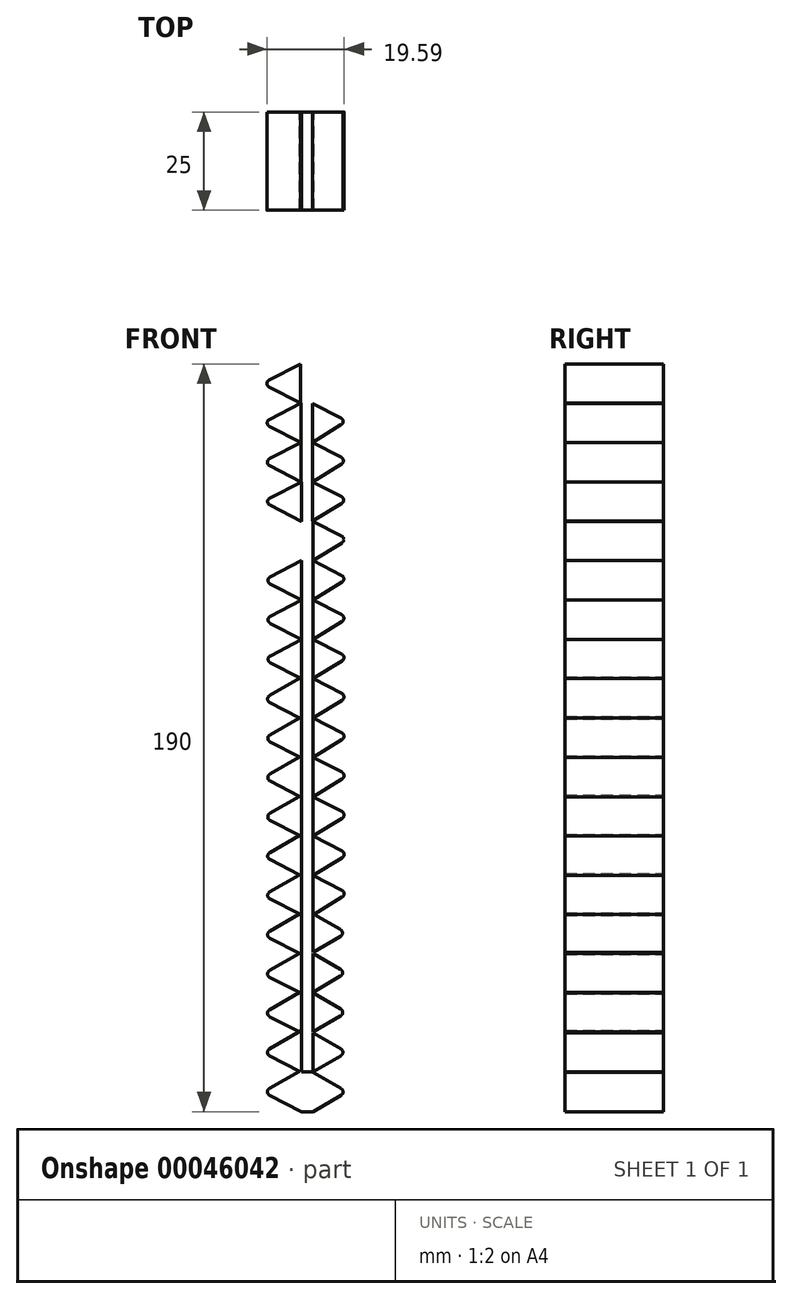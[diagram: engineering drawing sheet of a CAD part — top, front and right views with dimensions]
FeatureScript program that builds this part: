
annotation { "Feature Type Name" : "Feature", "Feature Type Description" : "" }
export const myFeature = defineFeature(function(context is Context, id is Id, definition is map)
    precondition{}
    {
        {
            var Q0;
            Q0=qCreatedBy(makeId("Front.planeOp"),FACE);
            var sketch = newSketch(context, id + "F0", { "sketchPlane" : qUnion([Q0])});
            skLineSegment(sketch, "E0.right", {"start": v(-51.03, -7.28) * mm, "end": v(-51.03, -157.28) * mm});
            skLineSegment(sketch, "E1", {"start": v(-51.03, -157.28) * mm, "end": v(-60.8, -152.28) * mm});
            skLineSegment(sketch, "E2", {"start": v(-60.8, -152.28) * mm, "end": v(-51.03, -146.64) * mm});
            skLineSegment(sketch, "E3.1.0.0", {"start": v(-60.8, -142.3) * mm, "end": v(-51.02, -136.66) * mm});
            skLineSegment(sketch, "E3.1.0.1", {"start": v(-51.02, -147.3) * mm, "end": v(-60.8, -142.3) * mm});
            skLineSegment(sketch, "E3.2.0.0", {"start": v(-60.78, -132.32) * mm, "end": v(-51, -126.68) * mm});
            skLineSegment(sketch, "E3.2.0.1", {"start": v(-51, -137.32) * mm, "end": v(-60.78, -132.32) * mm});
            skLineSegment(sketch, "E3.3.0.0", {"start": v(-60.77, -122.35) * mm, "end": v(-51, -116.7) * mm});
            skLineSegment(sketch, "E3.3.0.1", {"start": v(-51, -127.35) * mm, "end": v(-60.77, -122.35) * mm});
            skLineSegment(sketch, "E3.4.0.0", {"start": v(-60.76, -112.37) * mm, "end": v(-50.99, -106.72) * mm});
            skLineSegment(sketch, "E3.4.0.1", {"start": v(-50.99, -117.37) * mm, "end": v(-60.76, -112.37) * mm});
            skLineSegment(sketch, "E3.5.0.0", {"start": v(-60.75, -102.39) * mm, "end": v(-50.98, -96.75) * mm});
            skLineSegment(sketch, "E3.5.0.1", {"start": v(-50.98, -107.39) * mm, "end": v(-60.75, -102.39) * mm});
            skLineSegment(sketch, "E3.6.0.0", {"start": v(-60.74, -92.4) * mm, "end": v(-50.97, -86.77) * mm});
            skLineSegment(sketch, "E3.6.0.1", {"start": v(-50.97, -97.4) * mm, "end": v(-60.74, -92.4) * mm});
            skLineSegment(sketch, "E3.7.0.0", {"start": v(-60.73, -82.43) * mm, "end": v(-50.95, -76.79) * mm});
            skLineSegment(sketch, "E3.7.0.1", {"start": v(-50.95, -87.43) * mm, "end": v(-60.73, -82.43) * mm});
            skLineSegment(sketch, "E3.8.0.0", {"start": v(-60.72, -72.45) * mm, "end": v(-50.94, -66.8) * mm});
            skLineSegment(sketch, "E3.8.0.1", {"start": v(-50.94, -77.45) * mm, "end": v(-60.72, -72.45) * mm});
            skLineSegment(sketch, "E3.9.0.0", {"start": v(-60.7, -62.47) * mm, "end": v(-50.93, -56.83) * mm});
            skLineSegment(sketch, "E3.9.0.1", {"start": v(-50.93, -67.47) * mm, "end": v(-60.7, -62.47) * mm});
            skLineSegment(sketch, "E3.direction1", {"start": v(-60.8, -152.28) * mm, "end": v(-60.8, -142.3) * mm, "construction": true});
            skLineSegment(sketch, "E4.1.0.0", {"start": v(-60.77, -52.5) * mm, "end": v(-51, -46.86) * mm});
            skLineSegment(sketch, "E4.1.0.1", {"start": v(-51, -57.5) * mm, "end": v(-60.77, -52.5) * mm});
            skLineSegment(sketch, "E4.direction1", {"start": v(-60.7, -62.47) * mm, "end": v(-60.77, -52.5) * mm, "construction": true});
            skLineSegment(sketch, "E5", {"start": v(-51.03, -7.28) * mm, "end": v(-51.03, -17.28) * mm});
            skLineSegment(sketch, "E6", {"start": v(-51.03, -17.28) * mm, "end": v(-60.8, -12.28) * mm});
            skLineSegment(sketch, "E7", {"start": v(-60.8, -12.28) * mm, "end": v(-51.03, -7.28) * mm});
            skLineSegment(sketch, "E8", {"start": v(-51.03, -7.28) * mm, "end": v(-48.18, -7.28) * mm});
            skLineSegment(sketch, "E9", {"start": v(-48.18, -7.28) * mm, "end": v(-48.18, -157.28) * mm});
            skLineSegment(sketch, "E10", {"start": v(-48.18, -157.28) * mm, "end": v(-51.03, -157.28) * mm});
            skLineSegment(sketch, "E11", {"start": v(-48.18, -7.28) * mm, "end": v(-39.28, -11.84) * mm});
            skLineSegment(sketch, "E12", {"start": v(-39.28, -11.84) * mm, "end": v(-48.18, -17.28) * mm});
            skLineSegment(sketch, "E13", {"start": v(-48.18, -17.28) * mm, "end": v(-48.18, -7.28) * mm});
            skLineSegment(sketch, "E14.1.0.0", {"start": v(-48.18, -27.28) * mm, "end": v(-48.18, -17.28) * mm});
            skLineSegment(sketch, "E14.1.0.1", {"start": v(-48.18, -17.28) * mm, "end": v(-39.27, -21.84) * mm});
            skLineSegment(sketch, "E14.1.0.2", {"start": v(-39.27, -21.84) * mm, "end": v(-48.18, -27.28) * mm});
            skLineSegment(sketch, "E14.2.0.0", {"start": v(-48.17, -37.28) * mm, "end": v(-48.17, -27.28) * mm});
            skLineSegment(sketch, "E14.2.0.1", {"start": v(-48.17, -27.28) * mm, "end": v(-39.27, -31.84) * mm});
            skLineSegment(sketch, "E14.2.0.2", {"start": v(-39.27, -31.84) * mm, "end": v(-48.17, -37.28) * mm});
            skLineSegment(sketch, "E14.3.0.0", {"start": v(-48.16, -47.28) * mm, "end": v(-48.16, -37.28) * mm});
            skLineSegment(sketch, "E14.3.0.1", {"start": v(-48.16, -37.28) * mm, "end": v(-39.26, -41.84) * mm});
            skLineSegment(sketch, "E14.3.0.2", {"start": v(-39.26, -41.84) * mm, "end": v(-48.16, -47.28) * mm});
            skLineSegment(sketch, "E14.4.0.0", {"start": v(-48.15, -57.28) * mm, "end": v(-48.15, -47.28) * mm});
            skLineSegment(sketch, "E14.4.0.1", {"start": v(-48.15, -47.28) * mm, "end": v(-39.25, -51.84) * mm});
            skLineSegment(sketch, "E14.4.0.2", {"start": v(-39.25, -51.84) * mm, "end": v(-48.15, -57.28) * mm});
            skLineSegment(sketch, "E14.5.0.0", {"start": v(-48.14, -67.28) * mm, "end": v(-48.14, -57.28) * mm});
            skLineSegment(sketch, "E14.5.0.1", {"start": v(-48.14, -57.28) * mm, "end": v(-39.24, -61.84) * mm});
            skLineSegment(sketch, "E14.5.0.2", {"start": v(-39.24, -61.84) * mm, "end": v(-48.14, -67.28) * mm});
            skLineSegment(sketch, "E14.6.0.0", {"start": v(-48.14, -77.28) * mm, "end": v(-48.14, -67.28) * mm});
            skLineSegment(sketch, "E14.6.0.1", {"start": v(-48.14, -67.28) * mm, "end": v(-39.23, -71.84) * mm});
            skLineSegment(sketch, "E14.6.0.2", {"start": v(-39.23, -71.84) * mm, "end": v(-48.14, -77.28) * mm});
            skLineSegment(sketch, "E14.7.0.0", {"start": v(-48.13, -87.28) * mm, "end": v(-48.13, -77.28) * mm});
            skLineSegment(sketch, "E14.7.0.1", {"start": v(-48.13, -77.28) * mm, "end": v(-39.23, -81.84) * mm});
            skLineSegment(sketch, "E14.7.0.2", {"start": v(-39.23, -81.84) * mm, "end": v(-48.13, -87.28) * mm});
            skLineSegment(sketch, "E14.8.0.0", {"start": v(-48.12, -97.28) * mm, "end": v(-48.12, -87.28) * mm});
            skLineSegment(sketch, "E14.8.0.1", {"start": v(-48.12, -87.28) * mm, "end": v(-39.22, -91.84) * mm});
            skLineSegment(sketch, "E14.8.0.2", {"start": v(-39.22, -91.84) * mm, "end": v(-48.12, -97.28) * mm});
            skLineSegment(sketch, "E14.9.0.0", {"start": v(-48.11, -107.28) * mm, "end": v(-48.11, -97.28) * mm});
            skLineSegment(sketch, "E14.9.0.1", {"start": v(-48.11, -97.28) * mm, "end": v(-39.21, -101.84) * mm});
            skLineSegment(sketch, "E14.9.0.2", {"start": v(-39.21, -101.84) * mm, "end": v(-48.11, -107.28) * mm});
            skLineSegment(sketch, "E14.direction1", {"start": v(-48.18, -17.28) * mm, "end": v(-48.18, -27.28) * mm, "construction": true});
            skLineSegment(sketch, "E15", {"start": v(-48.18, -157.28) * mm, "end": v(-39.52, -152.28) * mm});
            skLineSegment(sketch, "E16", {"start": v(-39.52, -152.28) * mm, "end": v(-48.18, -147.3) * mm});
            skLineSegment(sketch, "E17", {"start": v(-48.18, -147.3) * mm, "end": v(-48.18, -157.28) * mm});
            skLineSegment(sketch, "E18.1.0.0", {"start": v(-48.22, -147.18) * mm, "end": v(-51.06, -147.18) * mm});
            skLineSegment(sketch, "E18.1.0.1", {"start": v(-48.22, -147.18) * mm, "end": v(-39.56, -142.18) * mm});
            skLineSegment(sketch, "E18.1.0.2", {"start": v(-48.22, 2.82) * mm, "end": v(-48.22, -147.18) * mm});
            skLineSegment(sketch, "E18.1.0.3", {"start": v(-39.56, -142.18) * mm, "end": v(-48.22, -137.2) * mm});
            skLineSegment(sketch, "E18.1.0.4", {"start": v(-48.22, -137.2) * mm, "end": v(-48.22, -147.18) * mm});
            skLineSegment(sketch, "E18.2.0.0", {"start": v(-48.26, -137.08) * mm, "end": v(-51.1, -137.08) * mm});
            skLineSegment(sketch, "E18.2.0.1", {"start": v(-48.26, -137.08) * mm, "end": v(-39.6, -132.08) * mm});
            skLineSegment(sketch, "E18.2.0.2", {"start": v(-48.26, 12.92) * mm, "end": v(-48.26, -137.08) * mm});
            skLineSegment(sketch, "E18.2.0.3", {"start": v(-39.6, -132.08) * mm, "end": v(-48.26, -127.1) * mm});
            skLineSegment(sketch, "E18.2.0.4", {"start": v(-48.26, -127.1) * mm, "end": v(-48.26, -137.08) * mm});
            skLineSegment(sketch, "E18.3.0.0", {"start": v(-48.3, -126.98) * mm, "end": v(-51.13, -126.98) * mm});
            skLineSegment(sketch, "E18.3.0.1", {"start": v(-48.3, -126.98) * mm, "end": v(-39.63, -121.98) * mm});
            skLineSegment(sketch, "E18.3.0.2", {"start": v(-48.3, 23.02) * mm, "end": v(-48.3, -126.98) * mm});
            skLineSegment(sketch, "E18.3.0.3", {"start": v(-39.63, -121.98) * mm, "end": v(-48.3, -117) * mm});
            skLineSegment(sketch, "E18.3.0.4", {"start": v(-48.3, -117) * mm, "end": v(-48.3, -126.98) * mm});
            skLineSegment(sketch, "E18.4.0.0", {"start": v(-48.33, -116.88) * mm, "end": v(-51.17, -116.88) * mm});
            skLineSegment(sketch, "E18.4.0.1", {"start": v(-48.33, -116.88) * mm, "end": v(-39.67, -111.88) * mm});
            skLineSegment(sketch, "E18.4.0.2", {"start": v(-48.33, 33.12) * mm, "end": v(-48.33, -116.88) * mm});
            skLineSegment(sketch, "E18.4.0.3", {"start": v(-39.67, -111.88) * mm, "end": v(-48.33, -106.9) * mm});
            skLineSegment(sketch, "E18.4.0.4", {"start": v(-48.33, -106.9) * mm, "end": v(-48.33, -116.88) * mm});
            skLineSegment(sketch, "E18.direction1", {"start": v(-51.03, -157.28) * mm, "end": v(-51.06, -147.18) * mm, "construction": true});
            skLineSegment(sketch, "E19.1.0.0", {"start": v(-51, -27.3) * mm, "end": v(-60.78, -22.3) * mm});
            skLineSegment(sketch, "E19.1.0.1", {"start": v(-60.78, -22.3) * mm, "end": v(-51, -17.3) * mm});
            skLineSegment(sketch, "E19.1.0.2", {"start": v(-51, -17.3) * mm, "end": v(-51, -27.3) * mm});
            skLineSegment(sketch, "E19.2.0.0", {"start": v(-50.98, -37.32) * mm, "end": v(-60.76, -32.32) * mm});
            skLineSegment(sketch, "E19.2.0.1", {"start": v(-60.76, -32.32) * mm, "end": v(-50.98, -27.32) * mm});
            skLineSegment(sketch, "E19.2.0.2", {"start": v(-50.98, -27.32) * mm, "end": v(-50.98, -37.32) * mm});
            skLineSegment(sketch, "E19.3.0.0", {"start": v(-50.96, -47.34) * mm, "end": v(-60.73, -42.34) * mm});
            skLineSegment(sketch, "E19.3.0.1", {"start": v(-60.73, -42.34) * mm, "end": v(-50.96, -37.34) * mm});
            skLineSegment(sketch, "E19.3.0.2", {"start": v(-50.96, -37.34) * mm, "end": v(-50.96, -47.34) * mm});
            skLineSegment(sketch, "E19.direction1", {"start": v(-60.8, -12.28) * mm, "end": v(-60.78, -22.3) * mm, "construction": true});
            skLineSegment(sketch, "E20.bottom", {"start": v(-51.03, -7.28) * mm, "end": v(-48.33, -7.28) * mm});
            skLineSegment(sketch, "E20.top", {"start": v(-51.03, 33.12) * mm, "end": v(-48.33, 33.12) * mm});
            skLineSegment(sketch, "E20.left", {"start": v(-51.03, -7.28) * mm, "end": v(-51.03, 33.12) * mm});
            skLineSegment(sketch, "E20.right", {"start": v(-48.33, -7.28) * mm, "end": v(-48.33, 33.12) * mm});
            skLineSegment(sketch, "E21.1.0.0", {"start": v(-48.24, 2.72) * mm, "end": v(-39.34, -1.84) * mm});
            skLineSegment(sketch, "E21.1.0.1", {"start": v(-39.34, -1.84) * mm, "end": v(-48.24, -7.28) * mm});
            skLineSegment(sketch, "E21.1.0.2", {"start": v(-48.24, -7.28) * mm, "end": v(-48.24, 2.72) * mm});
            skLineSegment(sketch, "E21.1.0.3", {"start": v(-51.09, 2.72) * mm, "end": v(-51.09, -7.28) * mm});
            skLineSegment(sketch, "E21.1.0.4", {"start": v(-60.86, -2.28) * mm, "end": v(-51.09, 2.72) * mm});
            skLineSegment(sketch, "E21.1.0.5", {"start": v(-51.09, -7.28) * mm, "end": v(-60.86, -2.28) * mm});
            skLineSegment(sketch, "E21.1.0.6", {"start": v(-51.09, 2.72) * mm, "end": v(-48.39, 2.72) * mm});
            skLineSegment(sketch, "E21.1.0.7", {"start": v(-51.09, 2.72) * mm, "end": v(-48.24, 2.72) * mm});
            skLineSegment(sketch, "E21.2.0.0", {"start": v(-48.3, 12.72) * mm, "end": v(-39.4, 8.16) * mm});
            skLineSegment(sketch, "E21.2.0.1", {"start": v(-39.4, 8.16) * mm, "end": v(-48.3, 2.72) * mm});
            skLineSegment(sketch, "E21.2.0.2", {"start": v(-48.3, 2.72) * mm, "end": v(-48.3, 12.72) * mm});
            skLineSegment(sketch, "E21.2.0.3", {"start": v(-51.14, 12.72) * mm, "end": v(-51.14, 2.72) * mm});
            skLineSegment(sketch, "E21.2.0.4", {"start": v(-60.92, 7.72) * mm, "end": v(-51.14, 12.72) * mm});
            skLineSegment(sketch, "E21.2.0.5", {"start": v(-51.14, 2.72) * mm, "end": v(-60.92, 7.72) * mm});
            skLineSegment(sketch, "E21.2.0.6", {"start": v(-51.14, 12.72) * mm, "end": v(-48.44, 12.72) * mm});
            skLineSegment(sketch, "E21.2.0.7", {"start": v(-51.14, 12.72) * mm, "end": v(-48.3, 12.72) * mm});
            skLineSegment(sketch, "E21.3.0.0", {"start": v(-48.36, 22.72) * mm, "end": v(-39.46, 18.16) * mm});
            skLineSegment(sketch, "E21.3.0.1", {"start": v(-39.46, 18.16) * mm, "end": v(-48.36, 12.72) * mm});
            skLineSegment(sketch, "E21.3.0.2", {"start": v(-48.36, 12.72) * mm, "end": v(-48.36, 22.72) * mm});
            skLineSegment(sketch, "E21.3.0.3", {"start": v(-51.2, 22.72) * mm, "end": v(-51.2, 12.72) * mm});
            skLineSegment(sketch, "E21.3.0.4", {"start": v(-60.98, 17.72) * mm, "end": v(-51.2, 22.72) * mm});
            skLineSegment(sketch, "E21.3.0.5", {"start": v(-51.2, 12.72) * mm, "end": v(-60.98, 17.72) * mm});
            skLineSegment(sketch, "E21.3.0.6", {"start": v(-51.2, 22.72) * mm, "end": v(-48.5, 22.72) * mm});
            skLineSegment(sketch, "E21.3.0.7", {"start": v(-51.2, 22.72) * mm, "end": v(-48.36, 22.72) * mm});
            skLineSegment(sketch, "E21.4.0.0", {"start": v(-48.42, 32.72) * mm, "end": v(-39.51, 28.16) * mm});
            skLineSegment(sketch, "E21.4.0.1", {"start": v(-39.51, 28.16) * mm, "end": v(-48.42, 22.72) * mm});
            skLineSegment(sketch, "E21.4.0.2", {"start": v(-48.42, 22.72) * mm, "end": v(-48.42, 32.72) * mm});
            skLineSegment(sketch, "E21.4.0.3", {"start": v(-51.26, 32.72) * mm, "end": v(-51.26, 22.72) * mm});
            skLineSegment(sketch, "E21.4.0.4", {"start": v(-61.03, 27.72) * mm, "end": v(-51.26, 32.72) * mm});
            skLineSegment(sketch, "E21.4.0.5", {"start": v(-51.26, 22.72) * mm, "end": v(-61.03, 27.72) * mm});
            skLineSegment(sketch, "E21.4.0.6", {"start": v(-51.26, 32.72) * mm, "end": v(-48.56, 32.72) * mm});
            skLineSegment(sketch, "E21.4.0.7", {"start": v(-51.26, 32.72) * mm, "end": v(-48.42, 32.72) * mm});
            skLineSegment(sketch, "E21.direction1", {"start": v(-48.18, -7.28) * mm, "end": v(-48.24, 2.72) * mm, "construction": true});
            skSolve(sketch);
        }
        {
            var Q0;
            {var subQ1=sQuery(id+"F0.wireOp",EDGE,"E5");Q0=makeQuery(id+"F0.imprint","IMPRINT",FACE,{"disambiguationData":[TD([[makeQuery(id+"F0.imprint","IMPRINT",EDGE,{"derivedFrom":subQ1}),1.0]])]});}
            var Q1;
            {var subQ8=sQuery(id+"F0.wireOp",EDGE,"E18.3.0.4");Q1=makeQuery(id+"F0.imprint","IMPRINT",FACE,{"disambiguationData":[TD([[makeQuery(id+"F0.imprint","IMPRINT",EDGE,{"derivedFrom":subQ8}),-1.0]])]});}
            var Q2;
            {var subQ5=sQuery(id+"F0.wireOp",EDGE,"E18.2.0.4");Q2=makeQuery(id+"F0.imprint","IMPRINT",FACE,{"disambiguationData":[TD([[makeQuery(id+"F0.imprint","IMPRINT",EDGE,{"derivedFrom":subQ5}),-1.0]])]});}
            var Q3;
            {var subQ0=sQuery(id+"F0.wireOp",EDGE,"E18.1.0.4");Q3=makeQuery(id+"F0.imprint","IMPRINT",FACE,{"disambiguationData":[TD([[makeQuery(id+"F0.imprint","IMPRINT",EDGE,{"derivedFrom":subQ0}),-1.0]])]});}
            var Q4;
            {var subQ6=sQuery(id+"F0.wireOp",EDGE,"E10");Q4=makeQuery(id+"F0.imprint","IMPRINT",FACE,{"disambiguationData":[TD([[makeQuery(id+"F0.imprint","IMPRINT",EDGE,{"derivedFrom":subQ6}),-1.0]])]});}
            extrude(context, id + "F1", {"entities" : qUnion([Q0, Q1, Q2, Q3, Q4]), "depth" : 25 * mm});
        }
        {
            var Q0;
            Q0=makeQuery(id+"F0.imprint","IMPRINT",FACE,{"disambiguationData":[TD([[makeQuery(id+"F0.imprint","IMPRINT",EDGE,{"derivedFrom":sQuery(id+"F0.wireOp",EDGE,"E11")}),-1.0]])]});
            var Q1;
            Q1=makeQuery(id+"F0.imprint","IMPRINT",FACE,{"disambiguationData":[TD([[makeQuery(id+"F0.imprint","IMPRINT",EDGE,{"derivedFrom":sQuery(id+"F0.wireOp",EDGE,"E14.1.0.0")}),-1.0]])]});
            var Q2;
            Q2=makeQuery(id+"F0.imprint","IMPRINT",FACE,{"disambiguationData":[TD([[makeQuery(id+"F0.imprint","IMPRINT",EDGE,{"derivedFrom":sQuery(id+"F0.wireOp",EDGE,"E14.2.0.0")}),-1.0]])]});
            var Q3;
            Q3=makeQuery(id+"F0.imprint","IMPRINT",FACE,{"disambiguationData":[TD([[makeQuery(id+"F0.imprint","IMPRINT",EDGE,{"derivedFrom":sQuery(id+"F0.wireOp",EDGE,"E14.3.0.0")}),-1.0]])]});
            var Q4;
            Q4=makeQuery(id+"F0.imprint","IMPRINT",FACE,{"disambiguationData":[TD([[makeQuery(id+"F0.imprint","IMPRINT",EDGE,{"derivedFrom":sQuery(id+"F0.wireOp",EDGE,"E14.4.0.0")}),-1.0]])]});
            var Q5;
            Q5=makeQuery(id+"F0.imprint","IMPRINT",FACE,{"disambiguationData":[TD([[makeQuery(id+"F0.imprint","IMPRINT",EDGE,{"derivedFrom":sQuery(id+"F0.wireOp",EDGE,"E14.5.0.0")}),-1.0]])]});
            var Q6;
            Q6=makeQuery(id+"F0.imprint","IMPRINT",FACE,{"disambiguationData":[TD([[makeQuery(id+"F0.imprint","IMPRINT",EDGE,{"derivedFrom":sQuery(id+"F0.wireOp",EDGE,"E14.6.0.0")}),-1.0]])]});
            var Q7;
            Q7=makeQuery(id+"F0.imprint","IMPRINT",FACE,{"disambiguationData":[TD([[makeQuery(id+"F0.imprint","IMPRINT",EDGE,{"derivedFrom":sQuery(id+"F0.wireOp",EDGE,"E14.7.0.0")}),-1.0]])]});
            var Q8;
            Q8=makeQuery(id+"F0.imprint","IMPRINT",FACE,{"disambiguationData":[TD([[makeQuery(id+"F0.imprint","IMPRINT",EDGE,{"derivedFrom":sQuery(id+"F0.wireOp",EDGE,"E14.8.0.0")}),-1.0]])]});
            var Q9;
            {var subQ0=sQuery(id+"F0.wireOp",EDGE,"E14.9.0.1");Q9=makeQuery(id+"F0.imprint","IMPRINT",FACE,{"disambiguationData":[TD([[makeQuery(id+"F0.imprint","IMPRINT",EDGE,{"derivedFrom":subQ0}),-1.0]])]});}
            extrude(context, id + "F2", {"entities" : qUnion([Q0, Q1, Q2, Q3, Q4, Q5, Q6, Q7, Q8, Q9]), "depth" : 25 * mm});
        }
        {
            var Q0;
            {var subQ0=sQuery(id+"F0.wireOp",EDGE,"E18.4.0.3");var subQ3=sQuery(id+"F0.wireOp",EDGE,"E9");var subQ10=makeQuery(id+"F0.imprint","INTERSECT",VERTEX,{"derivedFrom":[subQ3,subQ0]});Q0=makeQuery(id+"F0.imprint","IMPRINT",FACE,{"disambiguationData":[TD([[makeQuery(id+"F0.imprint","IMPRINT",EDGE,{"disambiguationData":[TD([[subQ10,-1.0]])],"derivedFrom":subQ3}),1.0]])]});}
            var Q1;
            {var subQ0=sQuery(id+"F0.wireOp",EDGE,"E18.3.0.3");var subQ1=sQuery(id+"F0.wireOp",EDGE,"E9");var subQ2=makeQuery(id+"F0.imprint","INTERSECT",VERTEX,{"derivedFrom":[subQ1,subQ0]});Q1=makeQuery(id+"F0.imprint","IMPRINT",FACE,{"disambiguationData":[TD([[makeQuery(id+"F0.imprint","IMPRINT",EDGE,{"disambiguationData":[TD([[subQ2,-1.0]])],"derivedFrom":subQ1}),1.0]])]});}
            var Q2;
            {var subQ0=sQuery(id+"F0.wireOp",EDGE,"E18.2.0.3");var subQ1=sQuery(id+"F0.wireOp",EDGE,"E9");var subQ2=makeQuery(id+"F0.imprint","INTERSECT",VERTEX,{"derivedFrom":[subQ1,subQ0]});Q2=makeQuery(id+"F0.imprint","IMPRINT",FACE,{"disambiguationData":[TD([[makeQuery(id+"F0.imprint","IMPRINT",EDGE,{"disambiguationData":[TD([[subQ2,-1.0]])],"derivedFrom":subQ1}),1.0]])]});}
            var Q3;
            {var subQ0=sQuery(id+"F0.wireOp",EDGE,"E18.1.0.3");var subQ1=sQuery(id+"F0.wireOp",EDGE,"E9");var subQ2=makeQuery(id+"F0.imprint","INTERSECT",VERTEX,{"derivedFrom":[subQ1,subQ0]});Q3=makeQuery(id+"F0.imprint","IMPRINT",FACE,{"disambiguationData":[TD([[makeQuery(id+"F0.imprint","IMPRINT",EDGE,{"disambiguationData":[TD([[subQ2,-1.0]])],"derivedFrom":subQ1}),1.0]])]});}
            var Q4;
            Q4=makeQuery(id+"F0.imprint","IMPRINT",FACE,{"disambiguationData":[TD([[makeQuery(id+"F0.imprint","IMPRINT",EDGE,{"derivedFrom":sQuery(id+"F0.wireOp",EDGE,"E15")}),1.0]])]});
            extrude(context, id + "F3", {"entities" : qUnion([Q0, Q1, Q2, Q3, Q4]), "operationType" : NewBodyOperationType.ADD, "depth" : 25 * mm});
        }
        {
            var Q0;
            Q0=makeQuery(id+"F0.imprint","IMPRINT",FACE,{"disambiguationData":[TD([[makeQuery(id+"F0.imprint","IMPRINT",EDGE,{"derivedFrom":sQuery(id+"F0.wireOp",EDGE,"E5")}),-1.0]])]});
            var Q1;
            Q1=makeQuery(id+"F0.imprint","IMPRINT",FACE,{"disambiguationData":[TD([[makeQuery(id+"F0.imprint","IMPRINT",EDGE,{"derivedFrom":sQuery(id+"F0.wireOp",EDGE,"557b663e-1838-4c1d-b6f1-36c1444994e9.1.0.1")}),-1.0]])]});
            var Q2;
            Q2=makeQuery(id+"F0.imprint","IMPRINT",FACE,{"disambiguationData":[TD([[makeQuery(id+"F0.imprint","IMPRINT",EDGE,{"derivedFrom":sQuery(id+"F0.wireOp",EDGE,"557b663e-1838-4c1d-b6f1-36c1444994e9.2.0.1")}),-1.0]])]});
            var Q3;
            Q3=makeQuery(id+"F0.imprint","IMPRINT",FACE,{"disambiguationData":[TD([[makeQuery(id+"F0.imprint","IMPRINT",EDGE,{"derivedFrom":sQuery(id+"F0.wireOp",EDGE,"557b663e-1838-4c1d-b6f1-36c1444994e9.3.0.1")}),-1.0]])]});
            var Q4;
            {var subQ0=sQuery(id+"F0.wireOp",EDGE,"E4.1.0.0");var subQ1=sQuery(id+"F0.wireOp",EDGE,"E0.right");var subQ2=makeQuery(id+"F0.imprint","INTERSECT",VERTEX,{"derivedFrom":[subQ1,subQ0]});Q4=makeQuery(id+"F0.imprint","IMPRINT",FACE,{"disambiguationData":[TD([[makeQuery(id+"F0.imprint","IMPRINT",EDGE,{"disambiguationData":[TD([[subQ2,-1.0]])],"derivedFrom":subQ1}),-1.0]])]});}
            var Q5;
            {var subQ0=sQuery(id+"F0.wireOp",EDGE,"E3.9.0.0");var subQ1=sQuery(id+"F0.wireOp",EDGE,"E0.right");var subQ2=makeQuery(id+"F0.imprint","INTERSECT",VERTEX,{"derivedFrom":[subQ1,subQ0]});Q5=makeQuery(id+"F0.imprint","IMPRINT",FACE,{"disambiguationData":[TD([[makeQuery(id+"F0.imprint","IMPRINT",EDGE,{"disambiguationData":[TD([[subQ2,-1.0]])],"derivedFrom":subQ1}),-1.0]])]});}
            var Q6;
            {var subQ0=sQuery(id+"F0.wireOp",EDGE,"E3.8.0.0");var subQ1=sQuery(id+"F0.wireOp",EDGE,"E0.right");var subQ2=makeQuery(id+"F0.imprint","INTERSECT",VERTEX,{"derivedFrom":[subQ1,subQ0]});Q6=makeQuery(id+"F0.imprint","IMPRINT",FACE,{"disambiguationData":[TD([[makeQuery(id+"F0.imprint","IMPRINT",EDGE,{"disambiguationData":[TD([[subQ2,-1.0]])],"derivedFrom":subQ1}),-1.0]])]});}
            var Q7;
            {var subQ0=sQuery(id+"F0.wireOp",EDGE,"E3.7.0.0");var subQ1=sQuery(id+"F0.wireOp",EDGE,"E0.right");var subQ2=makeQuery(id+"F0.imprint","INTERSECT",VERTEX,{"derivedFrom":[subQ1,subQ0]});Q7=makeQuery(id+"F0.imprint","IMPRINT",FACE,{"disambiguationData":[TD([[makeQuery(id+"F0.imprint","IMPRINT",EDGE,{"disambiguationData":[TD([[subQ2,-1.0]])],"derivedFrom":subQ1}),-1.0]])]});}
            extrude(context, id + "F4", {"entities" : qUnion([Q0, Q1, Q2, Q3, Q4, Q5, Q6, Q7]), "operationType" : NewBodyOperationType.ADD, "depth" : 25 * mm});
        }
        {
            var Q0;
            {var subQ0=sQuery(id+"F0.wireOp",EDGE,"E3.6.0.0");var subQ1=sQuery(id+"F0.wireOp",EDGE,"E0.right");var subQ2=makeQuery(id+"F0.imprint","INTERSECT",VERTEX,{"derivedFrom":[subQ1,subQ0]});Q0=makeQuery(id+"F0.imprint","IMPRINT",FACE,{"disambiguationData":[TD([[makeQuery(id+"F0.imprint","IMPRINT",EDGE,{"disambiguationData":[TD([[subQ2,-1.0]])],"derivedFrom":subQ1}),-1.0]])]});}
            var Q1;
            {var subQ0=sQuery(id+"F0.wireOp",EDGE,"E3.5.0.0");var subQ1=sQuery(id+"F0.wireOp",EDGE,"E0.right");var subQ2=makeQuery(id+"F0.imprint","INTERSECT",VERTEX,{"derivedFrom":[subQ1,subQ0]});Q1=makeQuery(id+"F0.imprint","IMPRINT",FACE,{"disambiguationData":[TD([[makeQuery(id+"F0.imprint","IMPRINT",EDGE,{"disambiguationData":[TD([[subQ2,-1.0]])],"derivedFrom":subQ1}),-1.0]])]});}
            var Q2;
            {var subQ0=sQuery(id+"F0.wireOp",EDGE,"E3.4.0.0");var subQ1=sQuery(id+"F0.wireOp",EDGE,"E0.right");var subQ2=makeQuery(id+"F0.imprint","INTERSECT",VERTEX,{"derivedFrom":[subQ1,subQ0]});Q2=makeQuery(id+"F0.imprint","IMPRINT",FACE,{"disambiguationData":[TD([[makeQuery(id+"F0.imprint","IMPRINT",EDGE,{"disambiguationData":[TD([[subQ2,-1.0]])],"derivedFrom":subQ1}),-1.0]])]});}
            var Q3;
            {var subQ0=sQuery(id+"F0.wireOp",EDGE,"E3.3.0.0");var subQ1=sQuery(id+"F0.wireOp",EDGE,"E0.right");var subQ2=makeQuery(id+"F0.imprint","INTERSECT",VERTEX,{"derivedFrom":[subQ1,subQ0]});Q3=makeQuery(id+"F0.imprint","IMPRINT",FACE,{"disambiguationData":[TD([[makeQuery(id+"F0.imprint","IMPRINT",EDGE,{"disambiguationData":[TD([[subQ2,-1.0]])],"derivedFrom":subQ1}),-1.0]])]});}
            var Q4;
            {var subQ1=sQuery(id+"F0.wireOp",EDGE,"E3.2.0.0");var subQ3=sQuery(id+"F0.wireOp",EDGE,"E0.right");var subQ4=makeQuery(id+"F0.imprint","INTERSECT",VERTEX,{"derivedFrom":[subQ3,subQ1]});Q4=makeQuery(id+"F0.imprint","IMPRINT",FACE,{"disambiguationData":[TD([[makeQuery(id+"F0.imprint","IMPRINT",EDGE,{"disambiguationData":[TD([[subQ4,-1.0]])],"derivedFrom":subQ3}),-1.0]])]});}
            extrude(context, id + "F5", {"entities" : qUnion([Q0, Q1, Q2, Q3, Q4]), "operationType" : NewBodyOperationType.ADD, "depth" : 25 * mm});
        }
        {
            var Q0;
            {var subQ0=sQuery(id+"F0.wireOp",EDGE,"E1");Q0=makeQuery(id+"F0.imprint","IMPRINT",FACE,{"disambiguationData":[TD([[makeQuery(id+"F0.imprint","IMPRINT",EDGE,{"derivedFrom":subQ0}),-1.0]])]});}
            extrude(context, id + "F6", {"entities" : qUnion([Q0]), "operationType" : NewBodyOperationType.ADD, "depth" : 25 * mm});
        }
        {
            var Q0;
            {var subQ3=sQuery(id+"F0.wireOp",EDGE,"E3.2.0.1");var subQ6=sQuery(id+"F0.wireOp",EDGE,"E0.right");var subQ9=makeQuery(id+"F0.imprint","INTERSECT",VERTEX,{"derivedFrom":[subQ6,subQ3]});Q0=makeQuery(id+"F0.imprint","IMPRINT",FACE,{"disambiguationData":[TD([[makeQuery(id+"F0.imprint","IMPRINT",EDGE,{"disambiguationData":[TD([[subQ9,-1.0]])],"derivedFrom":subQ6}),-1.0]])]});}
            extrude(context, id + "F7", {"entities" : qUnion([Q0]), "depth" : 25 * mm});
        }
        {
            var Q0;
            Q0=makeQuery(id+"F2.opExtrude","SWEPT_EDGE",EDGE,{"disambiguationData":[OSD([sQuery(id+"F0.wireOp",EDGE,"E11"),sQuery(id+"F0.wireOp",EDGE,"E12")])]});
            var Q1;
            Q1=makeQuery(id+"F2.opExtrude","SWEPT_EDGE",EDGE,{"disambiguationData":[OSD([sQuery(id+"F0.wireOp",EDGE,"E14.1.0.1"),sQuery(id+"F0.wireOp",EDGE,"E14.1.0.2")])]});
            var Q2;
            Q2=makeQuery(id+"F2.opExtrude","SWEPT_EDGE",EDGE,{"disambiguationData":[OSD([sQuery(id+"F0.wireOp",EDGE,"E14.2.0.1"),sQuery(id+"F0.wireOp",EDGE,"E14.2.0.2")])]});
            var Q3;
            Q3=makeQuery(id+"F2.opExtrude","SWEPT_EDGE",EDGE,{"disambiguationData":[OSD([sQuery(id+"F0.wireOp",EDGE,"E14.3.0.1"),sQuery(id+"F0.wireOp",EDGE,"E14.3.0.2")])]});
            var Q4;
            Q4=makeQuery(id+"F2.opExtrude","SWEPT_EDGE",EDGE,{"disambiguationData":[OSD([sQuery(id+"F0.wireOp",EDGE,"E14.4.0.1"),sQuery(id+"F0.wireOp",EDGE,"E14.4.0.2")])]});
            var Q5;
            Q5=makeQuery(id+"F2.opExtrude","SWEPT_EDGE",EDGE,{"disambiguationData":[OSD([sQuery(id+"F0.wireOp",EDGE,"E14.5.0.1"),sQuery(id+"F0.wireOp",EDGE,"E14.5.0.2")])]});
            var Q6;
            Q6=makeQuery(id+"F2.opExtrude","SWEPT_EDGE",EDGE,{"disambiguationData":[OSD([sQuery(id+"F0.wireOp",EDGE,"E14.6.0.1"),sQuery(id+"F0.wireOp",EDGE,"E14.6.0.2")])]});
            var Q7;
            Q7=makeQuery(id+"F2.opExtrude","SWEPT_EDGE",EDGE,{"disambiguationData":[OSD([sQuery(id+"F0.wireOp",EDGE,"E14.7.0.1"),sQuery(id+"F0.wireOp",EDGE,"E14.7.0.2")])]});
            var Q8;
            Q8=makeQuery(id+"F2.opExtrude","SWEPT_EDGE",EDGE,{"disambiguationData":[OSD([sQuery(id+"F0.wireOp",EDGE,"E14.8.0.1"),sQuery(id+"F0.wireOp",EDGE,"E14.8.0.2")])]});
            var Q9;
            Q9=makeQuery(id+"F2.opExtrude","SWEPT_EDGE",EDGE,{"disambiguationData":[OSD([sQuery(id+"F0.wireOp",EDGE,"E14.9.0.1"),sQuery(id+"F0.wireOp",EDGE,"E14.9.0.2")])]});
            var Q10;
            Q10=makeQuery(id+"F3.opExtrude","SWEPT_EDGE",EDGE,{"disambiguationData":[OSD([sQuery(id+"F0.wireOp",EDGE,"E18.4.0.1"),sQuery(id+"F0.wireOp",EDGE,"E18.4.0.3")])]});
            var Q11;
            Q11=makeQuery(id+"F3.opExtrude","SWEPT_EDGE",EDGE,{"disambiguationData":[OSD([sQuery(id+"F0.wireOp",EDGE,"E18.3.0.1"),sQuery(id+"F0.wireOp",EDGE,"E18.3.0.3")])]});
            var Q12;
            Q12=makeQuery(id+"F3.opExtrude","SWEPT_EDGE",EDGE,{"disambiguationData":[OSD([sQuery(id+"F0.wireOp",EDGE,"E18.2.0.1"),sQuery(id+"F0.wireOp",EDGE,"E18.2.0.3")])]});
            var Q13;
            Q13=makeQuery(id+"F3.opExtrude","SWEPT_EDGE",EDGE,{"disambiguationData":[OSD([sQuery(id+"F0.wireOp",EDGE,"E18.1.0.1"),sQuery(id+"F0.wireOp",EDGE,"E18.1.0.3")])]});
            var Q14;
            Q14=makeQuery(id+"F3.opExtrude","SWEPT_EDGE",EDGE,{"disambiguationData":[OSD([sQuery(id+"F0.wireOp",EDGE,"E15"),sQuery(id+"F0.wireOp",EDGE,"E16")])]});
            fillet(context, id + "F8", {"entities" : qUnion([Q0, Q1, Q2, Q3, Q4, Q5, Q6, Q7, Q8, Q9, Q10, Q11, Q12, Q13, Q14]), "radius" : 1 * mm, "tangentPropagation" : true, "allowEdgeOverflow" : false});
        }
        {
            var Q0;
            {var subQ0=sQuery(id+"F0.wireOp",EDGE,"557b663e-1838-4c1d-b6f1-36c1444994e9.1.0.2");var subQ1=sQuery(id+"F0.wireOp",EDGE,"E0.right");var subQ2=makeQuery(id+"F0.imprint","INTERSECT",VERTEX,{"derivedFrom":[subQ1,subQ0]});Q0=makeQuery(id+"F0.imprint","IMPRINT",FACE,{"disambiguationData":[TD([[makeQuery(id+"F0.imprint","IMPRINT",EDGE,{"disambiguationData":[TD([[subQ2,-1.0]])],"derivedFrom":subQ1}),-1.0]])]});}
            var Q1;
            {var subQ0=sQuery(id+"F0.wireOp",EDGE,"557b663e-1838-4c1d-b6f1-36c1444994e9.2.0.2");var subQ1=sQuery(id+"F0.wireOp",EDGE,"E0.right");var subQ2=makeQuery(id+"F0.imprint","INTERSECT",VERTEX,{"derivedFrom":[subQ1,subQ0]});Q1=makeQuery(id+"F0.imprint","IMPRINT",FACE,{"disambiguationData":[TD([[makeQuery(id+"F0.imprint","IMPRINT",EDGE,{"disambiguationData":[TD([[subQ2,-1.0]])],"derivedFrom":subQ1}),-1.0]])]});}
            var Q2;
            {var subQ0=sQuery(id+"F0.wireOp",EDGE,"557b663e-1838-4c1d-b6f1-36c1444994e9.3.0.2");var subQ1=sQuery(id+"F0.wireOp",EDGE,"E0.right");var subQ2=makeQuery(id+"F0.imprint","INTERSECT",VERTEX,{"derivedFrom":[subQ1,subQ0]});Q2=makeQuery(id+"F0.imprint","IMPRINT",FACE,{"disambiguationData":[TD([[makeQuery(id+"F0.imprint","IMPRINT",EDGE,{"disambiguationData":[TD([[subQ2,-1.0]])],"derivedFrom":subQ1}),-1.0]])]});}
            extrude(context, id + "F9", {"entities" : qUnion([Q0, Q1, Q2]), "operationType" : NewBodyOperationType.ADD, "depth" : 25 * mm});
        }
        {
            var Q0;
            {var subQ0=sQuery(id+"F0.wireOp",EDGE,"E19.1.0.1");var subQ1=sQuery(id+"F0.wireOp",EDGE,"E0.right");var subQ2=makeQuery(id+"F0.imprint","INTERSECT",VERTEX,{"derivedFrom":[subQ1,subQ0]});Q0=makeQuery(id+"F0.imprint","IMPRINT",FACE,{"disambiguationData":[TD([[makeQuery(id+"F0.imprint","IMPRINT",EDGE,{"disambiguationData":[TD([[subQ2,-1.0]])],"derivedFrom":subQ1}),-1.0]])]});}
            var Q1;
            {var subQ0=sQuery(id+"F0.wireOp",EDGE,"E19.2.0.1");var subQ1=sQuery(id+"F0.wireOp",EDGE,"E0.right");var subQ2=makeQuery(id+"F0.imprint","INTERSECT",VERTEX,{"derivedFrom":[subQ1,subQ0]});Q1=makeQuery(id+"F0.imprint","IMPRINT",FACE,{"disambiguationData":[TD([[makeQuery(id+"F0.imprint","IMPRINT",EDGE,{"disambiguationData":[TD([[subQ2,-1.0]])],"derivedFrom":subQ1}),-1.0]])]});}
            var Q2;
            {var subQ0=sQuery(id+"F0.wireOp",EDGE,"E19.3.0.1");var subQ1=sQuery(id+"F0.wireOp",EDGE,"E0.right");var subQ2=makeQuery(id+"F0.imprint","INTERSECT",VERTEX,{"derivedFrom":[subQ1,subQ0]});Q2=makeQuery(id+"F0.imprint","IMPRINT",FACE,{"disambiguationData":[TD([[makeQuery(id+"F0.imprint","IMPRINT",EDGE,{"disambiguationData":[TD([[subQ2,-1.0]])],"derivedFrom":subQ1}),-1.0]])]});}
            extrude(context, id + "F10", {"entities" : qUnion([Q0, Q1, Q2]), "depth" : 25 * mm});
        }
        {
            var Q0;
            Q0=makeQuery(id+"F10.opExtrude","SWEPT_EDGE",EDGE,{"disambiguationData":[OSD([sQuery(id+"F0.wireOp",EDGE,"E19.1.0.0"),sQuery(id+"F0.wireOp",EDGE,"E19.1.0.1")])]});
            var Q1;
            Q1=makeQuery(id+"F10.opExtrude","SWEPT_EDGE",EDGE,{"disambiguationData":[OSD([sQuery(id+"F0.wireOp",EDGE,"E19.2.0.0"),sQuery(id+"F0.wireOp",EDGE,"E19.2.0.1")])]});
            var Q2;
            Q2=makeQuery(id+"F10.opExtrude","SWEPT_EDGE",EDGE,{"disambiguationData":[OSD([sQuery(id+"F0.wireOp",EDGE,"E19.3.0.0"),sQuery(id+"F0.wireOp",EDGE,"E19.3.0.1")])]});
            fillet(context, id + "F11", {"entities" : qUnion([Q0, Q1, Q2]), "radius" : 1 * mm, "tangentPropagation" : true, "allowEdgeOverflow" : false});
        }
        {
            var Q0;
            {var subQ3=sQuery(id+"F0.wireOp",EDGE,"E3.9.0.0");var subQ5=sQuery(id+"F0.wireOp",EDGE,"E0.right");var subQ6=makeQuery(id+"F0.imprint","INTERSECT",VERTEX,{"derivedFrom":[subQ5,subQ3]});Q0=makeQuery(id+"F0.imprint","IMPRINT",FACE,{"disambiguationData":[TD([[makeQuery(id+"F0.imprint","IMPRINT",EDGE,{"disambiguationData":[TD([[subQ6,1.0]])],"derivedFrom":subQ5}),-1.0]])]});}
            var Q1;
            {var subQ5=sQuery(id+"F0.wireOp",EDGE,"E4.1.0.1");var subQ7=sQuery(id+"F0.wireOp",EDGE,"E0.right");var subQ8=makeQuery(id+"F0.imprint","INTERSECT",VERTEX,{"derivedFrom":[subQ7,subQ5]});Q1=makeQuery(id+"F0.imprint","IMPRINT",FACE,{"disambiguationData":[TD([[makeQuery(id+"F0.imprint","IMPRINT",EDGE,{"disambiguationData":[TD([[subQ8,-1.0]])],"derivedFrom":subQ7}),-1.0]])]});}
            var Q2;
            {var subQ5=sQuery(id+"F0.wireOp",EDGE,"E0.right");var subQ7=sQuery(id+"F0.wireOp",EDGE,"E3.9.0.1");var subQ9=makeQuery(id+"F0.imprint","INTERSECT",VERTEX,{"derivedFrom":[subQ5,subQ7]});Q2=makeQuery(id+"F0.imprint","IMPRINT",FACE,{"disambiguationData":[TD([[makeQuery(id+"F0.imprint","IMPRINT",EDGE,{"disambiguationData":[TD([[subQ9,-1.0]])],"derivedFrom":subQ5}),-1.0]])]});}
            var Q3;
            {var subQ5=sQuery(id+"F0.wireOp",EDGE,"E3.8.0.1");var subQ7=sQuery(id+"F0.wireOp",EDGE,"E0.right");var subQ9=makeQuery(id+"F0.imprint","INTERSECT",VERTEX,{"derivedFrom":[subQ7,subQ5]});Q3=makeQuery(id+"F0.imprint","IMPRINT",FACE,{"disambiguationData":[TD([[makeQuery(id+"F0.imprint","IMPRINT",EDGE,{"disambiguationData":[TD([[subQ9,-1.0]])],"derivedFrom":subQ7}),-1.0]])]});}
            var Q4;
            {var subQ3=sQuery(id+"F0.wireOp",EDGE,"E3.7.0.1");var subQ6=sQuery(id+"F0.wireOp",EDGE,"E0.right");var subQ9=makeQuery(id+"F0.imprint","INTERSECT",VERTEX,{"derivedFrom":[subQ6,subQ3]});Q4=makeQuery(id+"F0.imprint","IMPRINT",FACE,{"disambiguationData":[TD([[makeQuery(id+"F0.imprint","IMPRINT",EDGE,{"disambiguationData":[TD([[subQ9,-1.0]])],"derivedFrom":subQ6}),-1.0]])]});}
            var Q5;
            {var subQ3=sQuery(id+"F0.wireOp",EDGE,"E3.6.0.1");var subQ6=sQuery(id+"F0.wireOp",EDGE,"E0.right");var subQ9=makeQuery(id+"F0.imprint","INTERSECT",VERTEX,{"derivedFrom":[subQ6,subQ3]});Q5=makeQuery(id+"F0.imprint","IMPRINT",FACE,{"disambiguationData":[TD([[makeQuery(id+"F0.imprint","IMPRINT",EDGE,{"disambiguationData":[TD([[subQ9,-1.0]])],"derivedFrom":subQ6}),-1.0]])]});}
            var Q6;
            {var subQ3=sQuery(id+"F0.wireOp",EDGE,"E3.5.0.1");var subQ7=sQuery(id+"F0.wireOp",EDGE,"E0.right");var subQ10=makeQuery(id+"F0.imprint","INTERSECT",VERTEX,{"derivedFrom":[subQ7,subQ3]});Q6=makeQuery(id+"F0.imprint","IMPRINT",FACE,{"disambiguationData":[TD([[makeQuery(id+"F0.imprint","IMPRINT",EDGE,{"disambiguationData":[TD([[subQ10,-1.0]])],"derivedFrom":subQ7}),-1.0]])]});}
            var Q7;
            {var subQ5=sQuery(id+"F0.wireOp",EDGE,"E0.right");var subQ7=sQuery(id+"F0.wireOp",EDGE,"E3.4.0.1");var subQ8=makeQuery(id+"F0.imprint","INTERSECT",VERTEX,{"derivedFrom":[subQ5,subQ7]});Q7=makeQuery(id+"F0.imprint","IMPRINT",FACE,{"disambiguationData":[TD([[makeQuery(id+"F0.imprint","IMPRINT",EDGE,{"disambiguationData":[TD([[subQ8,-1.0]])],"derivedFrom":subQ5}),-1.0]])]});}
            var Q8;
            {var subQ5=sQuery(id+"F0.wireOp",EDGE,"E3.3.0.1");var subQ7=sQuery(id+"F0.wireOp",EDGE,"E0.right");var subQ8=makeQuery(id+"F0.imprint","INTERSECT",VERTEX,{"derivedFrom":[subQ7,subQ5]});Q8=makeQuery(id+"F0.imprint","IMPRINT",FACE,{"disambiguationData":[TD([[makeQuery(id+"F0.imprint","IMPRINT",EDGE,{"disambiguationData":[TD([[subQ8,-1.0]])],"derivedFrom":subQ7}),-1.0]])]});}
            extrude(context, id + "F12", {"entities" : qUnion([Q0, Q1, Q2, Q3, Q4, Q5, Q6, Q7, Q8]), "depth" : 25 * mm});
        }
        {
            var Q0;
            Q0=makeQuery(id+"F12.opExtrude","SWEPT_EDGE",EDGE,{"disambiguationData":[OSD([sQuery(id+"F0.wireOp",EDGE,"E4.1.0.0"),sQuery(id+"F0.wireOp",EDGE,"E4.1.0.1")])]});
            var Q1;
            Q1=makeQuery(id+"F12.opExtrude","SWEPT_EDGE",EDGE,{"disambiguationData":[OSD([sQuery(id+"F0.wireOp",EDGE,"E3.9.0.0"),sQuery(id+"F0.wireOp",EDGE,"E3.9.0.1")])]});
            var Q2;
            Q2=makeQuery(id+"F12.opExtrude","SWEPT_EDGE",EDGE,{"disambiguationData":[OSD([sQuery(id+"F0.wireOp",EDGE,"E3.8.0.0"),sQuery(id+"F0.wireOp",EDGE,"E3.8.0.1")])]});
            var Q3;
            Q3=makeQuery(id+"F12.opExtrude","SWEPT_EDGE",EDGE,{"disambiguationData":[OSD([sQuery(id+"F0.wireOp",EDGE,"E3.7.0.0"),sQuery(id+"F0.wireOp",EDGE,"E3.7.0.1")])]});
            var Q4;
            Q4=makeQuery(id+"F12.opExtrude","SWEPT_EDGE",EDGE,{"disambiguationData":[OSD([sQuery(id+"F0.wireOp",EDGE,"E3.6.0.0"),sQuery(id+"F0.wireOp",EDGE,"E3.6.0.1")])]});
            var Q5;
            Q5=makeQuery(id+"F12.opExtrude","SWEPT_EDGE",EDGE,{"disambiguationData":[OSD([sQuery(id+"F0.wireOp",EDGE,"E3.5.0.0"),sQuery(id+"F0.wireOp",EDGE,"E3.5.0.1")])]});
            var Q6;
            Q6=makeQuery(id+"F12.opExtrude","SWEPT_EDGE",EDGE,{"disambiguationData":[OSD([sQuery(id+"F0.wireOp",EDGE,"E3.4.0.0"),sQuery(id+"F0.wireOp",EDGE,"E3.4.0.1")])]});
            var Q7;
            Q7=makeQuery(id+"F12.opExtrude","SWEPT_EDGE",EDGE,{"disambiguationData":[OSD([sQuery(id+"F0.wireOp",EDGE,"E3.3.0.0"),sQuery(id+"F0.wireOp",EDGE,"E3.3.0.1")])]});
            var Q8;
            Q8=makeQuery(id+"F12.opExtrude","SWEPT_EDGE",EDGE,{"disambiguationData":[OSD([sQuery(id+"F0.wireOp",EDGE,"E3.2.0.0"),sQuery(id+"F0.wireOp",EDGE,"E3.2.0.1")])]});
            var Q9;
            Q9=makeQuery(id+"F7.opExtrude","SWEPT_EDGE",EDGE,{"disambiguationData":[OSD([sQuery(id+"F0.wireOp",EDGE,"E3.1.0.0"),sQuery(id+"F0.wireOp",EDGE,"E3.1.0.1")])]});
            var Q10;
            Q10=makeQuery(id+"F6.opExtrude","SWEPT_EDGE",EDGE,{"disambiguationData":[OSD([sQuery(id+"F0.wireOp",EDGE,"E1"),sQuery(id+"F0.wireOp",EDGE,"E2")])]});
            var Q11;
            Q11=makeQuery(id+"F4.opExtrude","SWEPT_EDGE",EDGE,{"disambiguationData":[OSD([sQuery(id+"F0.wireOp",EDGE,"E6"),sQuery(id+"F0.wireOp",EDGE,"E7")])]});
            fillet(context, id + "F13", {"entities" : qUnion([Q0, Q1, Q2, Q3, Q4, Q5, Q6, Q7, Q8, Q9, Q10, Q11]), "radius" : 1 * mm, "tangentPropagation" : true, "allowEdgeOverflow" : false});
        }
        {
            var Q0;
            Q0=makeQuery(id+"F0.imprint","IMPRINT",FACE,{"disambiguationData":[TD([[makeQuery(id+"F0.imprint","IMPRINT",EDGE,{"derivedFrom":sQuery(id+"F0.wireOp",EDGE,"E21.4.0.3")}),-1.0]])]});
            var Q1;
            Q1=makeQuery(id+"F0.imprint","IMPRINT",FACE,{"disambiguationData":[TD([[makeQuery(id+"F0.imprint","IMPRINT",EDGE,{"derivedFrom":sQuery(id+"F0.wireOp",EDGE,"E21.3.0.3")}),-1.0]])]});
            var Q2;
            Q2=makeQuery(id+"F0.imprint","IMPRINT",FACE,{"disambiguationData":[TD([[makeQuery(id+"F0.imprint","IMPRINT",EDGE,{"derivedFrom":sQuery(id+"F0.wireOp",EDGE,"E21.2.0.3")}),-1.0]])]});
            var Q3;
            {var subQ0=sQuery(id+"F0.wireOp",EDGE,"E21.2.0.0");var subQ1=sQuery(id+"F0.wireOp",EDGE,"E18.2.0.2");var subQ2=makeQuery(id+"F0.imprint","INTERSECT",VERTEX,{"derivedFrom":[subQ1,subQ0]});Q3=makeQuery(id+"F0.imprint","IMPRINT",FACE,{"disambiguationData":[TD([[makeQuery(id+"F0.imprint","IMPRINT",EDGE,{"disambiguationData":[TD([[subQ2,-1.0]])],"derivedFrom":subQ1}),1.0]])]});}
            extrude(context, id + "F14", {"entities" : qUnion([Q0, Q1, Q2, Q3]), "depth" : 25 * mm});
        }
        {
            var Q0;
            {var subQ0=sQuery(id+"F0.wireOp",EDGE,"E21.2.0.0");var subQ1=sQuery(id+"F0.wireOp",EDGE,"E18.2.0.2");var subQ2=makeQuery(id+"F0.imprint","INTERSECT",VERTEX,{"derivedFrom":[subQ1,subQ0]});Q0=makeQuery(id+"F0.imprint","IMPRINT",FACE,{"disambiguationData":[TD([[makeQuery(id+"F0.imprint","IMPRINT",EDGE,{"disambiguationData":[TD([[subQ2,-1.0]])],"derivedFrom":subQ1}),1.0]])]});}
            var Q1;
            {var subQ0=sQuery(id+"F0.wireOp",EDGE,"E21.1.0.0");var subQ1=sQuery(id+"F0.wireOp",EDGE,"E18.1.0.2");var subQ2=makeQuery(id+"F0.imprint","INTERSECT",VERTEX,{"derivedFrom":[subQ1,subQ0]});Q1=makeQuery(id+"F0.imprint","IMPRINT",FACE,{"disambiguationData":[TD([[makeQuery(id+"F0.imprint","IMPRINT",EDGE,{"disambiguationData":[TD([[subQ2,-1.0]])],"derivedFrom":subQ1}),1.0]])]});}
            var Q2;
            {var subQ0=sQuery(id+"F0.wireOp",EDGE,"E21.3.0.0");var subQ1=sQuery(id+"F0.wireOp",EDGE,"E18.3.0.2");var subQ2=makeQuery(id+"F0.imprint","INTERSECT",VERTEX,{"derivedFrom":[subQ1,subQ0]});Q2=makeQuery(id+"F0.imprint","IMPRINT",FACE,{"disambiguationData":[TD([[makeQuery(id+"F0.imprint","IMPRINT",EDGE,{"disambiguationData":[TD([[subQ2,-1.0]])],"derivedFrom":subQ1}),1.0]])]});}
            var Q3;
            {var subQ0=sQuery(id+"F0.wireOp",EDGE,"E21.4.0.0");var subQ1=sQuery(id+"F0.wireOp",EDGE,"E20.right");var subQ2=makeQuery(id+"F0.imprint","INTERSECT",VERTEX,{"derivedFrom":[subQ1,subQ0]});Q3=makeQuery(id+"F0.imprint","IMPRINT",FACE,{"disambiguationData":[TD([[makeQuery(id+"F0.imprint","IMPRINT",EDGE,{"disambiguationData":[TD([[subQ2,1.0]])],"derivedFrom":subQ1}),-1.0]])]});}
            extrude(context, id + "F15", {"entities" : qUnion([Q0, Q1, Q2, Q3]), "operationType" : NewBodyOperationType.ADD, "depth" : 25 * mm});
        }
        {
            var Q0;
            Q0=makeQuery(id+"F0.imprint","IMPRINT",FACE,{"disambiguationData":[TD([[makeQuery(id+"F0.imprint","IMPRINT",EDGE,{"derivedFrom":sQuery(id+"F0.wireOp",EDGE,"E21.1.0.3")}),-1.0]])]});
            var Q1;
            {var subQ5=sQuery(id+"F0.wireOp",EDGE,"E20.bottom");Q1=makeQuery(id+"F0.imprint","IMPRINT",FACE,{"disambiguationData":[TD([[makeQuery(id+"F0.imprint","IMPRINT",EDGE,{"derivedFrom":subQ5}),1.0]])]});}
            var Q2;
            {var subQ0=sQuery(id+"F0.wireOp",EDGE,"E21.1.0.7");var subQ1=makeQuery(id+"F0.imprint","IMPRINT",VERTEX,{"derivedFrom":subQ0});Q2=makeQuery(id+"F0.imprint","IMPRINT",FACE,{"disambiguationData":[TD([[makeQuery(id+"F0.imprint","IMPRINT",EDGE,{"disambiguationData":[TD([[subQ1,1.0]])],"derivedFrom":subQ0}),1.0]])]});}
            var Q3;
            {var subQ0=sQuery(id+"F0.wireOp",EDGE,"E21.2.0.7");var subQ1=makeQuery(id+"F0.imprint","IMPRINT",VERTEX,{"derivedFrom":subQ0});Q3=makeQuery(id+"F0.imprint","IMPRINT",FACE,{"disambiguationData":[TD([[makeQuery(id+"F0.imprint","IMPRINT",EDGE,{"disambiguationData":[TD([[subQ1,1.0]])],"derivedFrom":subQ0}),1.0]])]});}
            var Q4;
            {var subQ0=sQuery(id+"F0.wireOp",EDGE,"E21.3.0.7");var subQ1=makeQuery(id+"F0.imprint","IMPRINT",VERTEX,{"derivedFrom":subQ0});Q4=makeQuery(id+"F0.imprint","IMPRINT",FACE,{"disambiguationData":[TD([[makeQuery(id+"F0.imprint","IMPRINT",EDGE,{"disambiguationData":[TD([[subQ1,1.0]])],"derivedFrom":subQ0}),1.0]])]});}
            extrude(context, id + "F16", {"entities" : qUnion([Q0, Q1, Q2, Q3, Q4]), "operationType" : NewBodyOperationType.ADD, "depth" : 25 * mm});
        }
        {
            var Q0;
            Q0=makeQuery(id+"F14.opExtrude","SWEPT_EDGE",EDGE,{"disambiguationData":[OSD([sQuery(id+"F0.wireOp",EDGE,"E21.4.0.4"),sQuery(id+"F0.wireOp",EDGE,"E21.4.0.5")])]});
            var Q1;
            Q1=makeQuery(id+"F14.opExtrude","SWEPT_EDGE",EDGE,{"disambiguationData":[OSD([sQuery(id+"F0.wireOp",EDGE,"E21.3.0.4"),sQuery(id+"F0.wireOp",EDGE,"E21.3.0.5")])]});
            var Q2;
            Q2=makeQuery(id+"F14.opExtrude","SWEPT_EDGE",EDGE,{"disambiguationData":[OSD([sQuery(id+"F0.wireOp",EDGE,"E21.2.0.4"),sQuery(id+"F0.wireOp",EDGE,"E21.2.0.5")])]});
            var Q3;
            Q3=makeQuery(id+"F16.opExtrude","SWEPT_EDGE",EDGE,{"disambiguationData":[OSD([sQuery(id+"F0.wireOp",EDGE,"E21.1.0.4"),sQuery(id+"F0.wireOp",EDGE,"E21.1.0.5")])]});
            var Q4;
            Q4=makeQuery(id+"F15.opExtrude","SWEPT_EDGE",EDGE,{"disambiguationData":[OSD([sQuery(id+"F0.wireOp",EDGE,"E21.4.0.0"),sQuery(id+"F0.wireOp",EDGE,"E21.4.0.1")])]});
            var Q5;
            Q5=makeQuery(id+"F15.opExtrude","SWEPT_EDGE",EDGE,{"disambiguationData":[OSD([sQuery(id+"F0.wireOp",EDGE,"E21.3.0.0"),sQuery(id+"F0.wireOp",EDGE,"E21.3.0.1")])]});
            var Q6;
            Q6=makeQuery(id+"F14.opExtrude","SWEPT_EDGE",EDGE,{"disambiguationData":[OSD([sQuery(id+"F0.wireOp",EDGE,"E21.2.0.0"),sQuery(id+"F0.wireOp",EDGE,"E21.2.0.1")])]});
            var Q7;
            Q7=makeQuery(id+"F15.opExtrude","SWEPT_EDGE",EDGE,{"disambiguationData":[OSD([sQuery(id+"F0.wireOp",EDGE,"E21.1.0.0"),sQuery(id+"F0.wireOp",EDGE,"E21.1.0.1")])]});
            fillet(context, id + "F17", {"entities" : qUnion([Q0, Q1, Q2, Q3, Q4, Q5, Q6, Q7]), "radius" : 1 * mm, "tangentPropagation" : true, "allowEdgeOverflow" : false});
        }
    });
